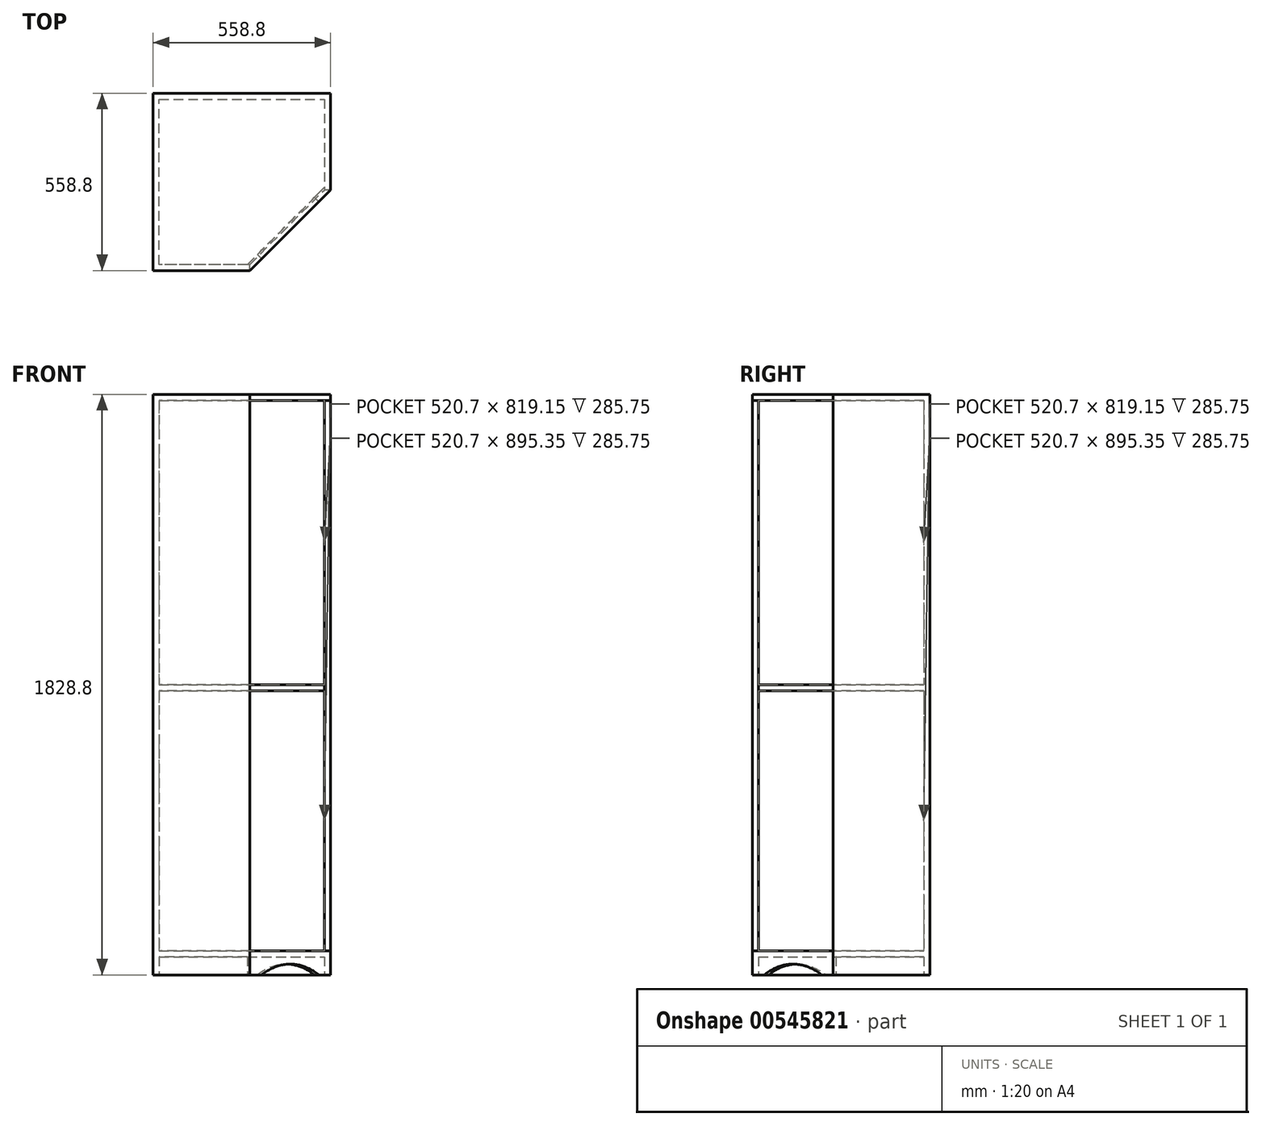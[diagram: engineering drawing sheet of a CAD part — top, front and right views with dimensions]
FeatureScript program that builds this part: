
annotation { "Feature Type Name" : "Feature", "Feature Type Description" : "" }
export const myFeature = defineFeature(function(context is Context, id is Id, definition is map)
    precondition{}
    {
        {
            var Q0;
            Q0=qCreatedBy(makeId("Top.planeOp"),FACE);
            var sketch = newSketch(context, id + "F0", { "sketchPlane" : qUnion([Q0])});
            skLineSegment(sketch, "E0", {"start": v(-279.4, 279.4) * mm, "end": v(279.4, 279.4) * mm});
            skLineSegment(sketch, "E1", {"start": v(279.4, 279.4) * mm, "end": v(279.4, -25.4) * mm});
            skLineSegment(sketch, "E2", {"start": v(279.4, -25.4) * mm, "end": v(25.4, -279.4) * mm, "construction": true});
            skLineSegment(sketch, "E3", {"start": v(25.4, -279.4) * mm, "end": v(-279.4, -279.4) * mm});
            skLineSegment(sketch, "E4", {"start": v(-279.4, -279.4) * mm, "end": v(-279.4, 279.4) * mm});
            skLineSegment(sketch, "E5", {"start": v(-279.4, -279.4) * mm, "end": v(279.4, 279.4) * mm, "construction": true});
            skLineSegment(sketch, "E6.0", {"start": v(260.35, 260.35) * mm, "end": v(260.35, -25.4) * mm});
            skLineSegment(sketch, "E6.1", {"start": v(-260.35, 260.35) * mm, "end": v(260.35, 260.35) * mm});
            skLineSegment(sketch, "E6.2", {"start": v(-260.35, -260.35) * mm, "end": v(-260.35, 260.35) * mm});
            skLineSegment(sketch, "E6.3", {"start": v(25.4, -260.35) * mm, "end": v(-260.35, -260.35) * mm});
            skLineSegment(sketch, "E7", {"start": v(279.4, -25.4) * mm, "end": v(260.35, -25.4) * mm});
            skLineSegment(sketch, "E8", {"start": v(25.4, -279.4) * mm, "end": v(25.4, -260.35) * mm});
            skSolve(sketch);
        }
        {
            var Q0;
            Q0=makeQuery(id+"F0.imprint","IMPRINT",FACE,{"disambiguationData":[TD([[makeQuery(id+"F0.imprint","IMPRINT",EDGE,{"derivedFrom":sQuery(id+"F0.wireOp",EDGE,"E0")}),-1.0]])]});
            var Q1;
            Q1 = qConstructionFilter(qBodyType(qCreatedBy(id + "F0" ,EDGE), BodyType.WIRE), ConstructionObject.NO);
            extrude(context, id + "F1", {"entities" : qUnion([Q0]), "surfaceEntities" : qUnion([Q1]), "depth" : 1828.8 * mm, "offsetDistance" : 25.4 * mm});
        }
        {
            var Q0;
            Q0=makeQuery(id+"F1.opExtrude","CAP_FACE",FACE,{"disambiguationData":[OSD([sQuery(id+"F0.wireOp",EDGE,"E0"),sQuery(id+"F0.wireOp",EDGE,"E1"),sQuery(id+"F0.wireOp",EDGE,"E3"),sQuery(id+"F0.wireOp",EDGE,"E4"),sQuery(id+"F0.wireOp",EDGE,"E6.0"),sQuery(id+"F0.wireOp",EDGE,"E6.1"),sQuery(id+"F0.wireOp",EDGE,"E6.2"),sQuery(id+"F0.wireOp",EDGE,"E6.3"),sQuery(id+"F0.wireOp",EDGE,"E7"),sQuery(id+"F0.wireOp",EDGE,"E8")])],"isStart":false});
            var sketch = newSketch(context, id + "F2", { "sketchPlane" : qUnion([Q0])});
            skLineSegment(sketch, "E9", {"start": v(25.4, -279.4) * mm, "end": v(279.4, -25.4) * mm});
            skLineSegment(sketch, "E10.0", {"start": v(25.4, -279.4) * mm, "end": v(-279.4, -279.4) * mm});
            skLineSegment(sketch, "E10.1", {"start": v(-279.4, -279.4) * mm, "end": v(-279.4, 279.4) * mm});
            skLineSegment(sketch, "E10.2", {"start": v(-279.4, 279.4) * mm, "end": v(279.4, 279.4) * mm});
            skLineSegment(sketch, "E10.3", {"start": v(279.4, 279.4) * mm, "end": v(279.4, -25.4) * mm});
            skSolve(sketch);
        }
        {
            var Q0;
            Q0 = qSketchRegion(id + "F2", true);
            extrude(context, id + "F3", {"entities" : qUnion([Q0]), "operationType" : NewBodyOperationType.ADD, "oppositeDirection" : true, "depth" : 19.05 * mm, "offsetDistance" : 25.4 * mm});
        }
        {
            var Q0;
            Q0=qCreatedBy(makeId("Top.planeOp"),FACE);
            var sketch = newSketch(context, id + "F4", { "sketchPlane" : qUnion([Q0])});
            skLineSegment(sketch, "E11.0", {"start": v(25.4, -279.4) * mm, "end": v(-279.4, -279.4) * mm});
            skLineSegment(sketch, "E11.1", {"start": v(279.4, 279.4) * mm, "end": v(279.4, -25.4) * mm});
            skLineSegment(sketch, "E11.2", {"start": v(-279.4, 279.4) * mm, "end": v(279.4, 279.4) * mm});
            skLineSegment(sketch, "E11.3", {"start": v(-279.4, -279.4) * mm, "end": v(-279.4, 279.4) * mm});
            skLineSegment(sketch, "E12", {"start": v(25.4, -279.4) * mm, "end": v(279.4, -25.4) * mm});
            skSolve(sketch);
        }
        {
            var Q0;
            Q0 = qSketchRegion(id + "F4", true);
            extrude(context, id + "F5", {"entities" : qUnion([Q0]), "operationType" : NewBodyOperationType.ADD, "depth" : 76.2 * mm, "offsetDistance" : 25.4 * mm});
        }
        {
            var Q0;
            Q0=makeQuery(id+"F5.boolean.opBoolean","MERGE",FACE,{"derivedFrom":[makeQuery(id+"F1.opExtrude","CAP_FACE",FACE,{"disambiguationData":[OSD([sQuery(id+"F0.wireOp",EDGE,"E0"),sQuery(id+"F0.wireOp",EDGE,"E1"),sQuery(id+"F0.wireOp",EDGE,"E3"),sQuery(id+"F0.wireOp",EDGE,"E4"),sQuery(id+"F0.wireOp",EDGE,"E6.0"),sQuery(id+"F0.wireOp",EDGE,"E6.1"),sQuery(id+"F0.wireOp",EDGE,"E6.2"),sQuery(id+"F0.wireOp",EDGE,"E6.3"),sQuery(id+"F0.wireOp",EDGE,"E7"),sQuery(id+"F0.wireOp",EDGE,"E8")])],"isStart":true}),makeQuery(id+"F5.opExtrude","CAP_FACE",FACE,{"disambiguationData":[OSD([sQuery(id+"F4.wireOp",EDGE,"E11.0"),sQuery(id+"F4.wireOp",EDGE,"E11.1"),sQuery(id+"F4.wireOp",EDGE,"E11.2"),sQuery(id+"F4.wireOp",EDGE,"E11.3"),sQuery(id+"F4.wireOp",EDGE,"E12")])],"isStart":true})]});
            var sketch = newSketch(context, id + "F6", { "sketchPlane" : qUnion([Q0])});
            skLineSegment(sketch, "E13.0", {"start": v(260.35, -260.35) * mm, "end": v(260.35, 17.5) * mm});
            skLineSegment(sketch, "E13.1", {"start": v(17.5, 260.35) * mm, "end": v(260.35, 17.5) * mm});
            skLineSegment(sketch, "E13.2", {"start": v(-260.35, -260.35) * mm, "end": v(260.35, -260.35) * mm});
            skLineSegment(sketch, "E13.3", {"start": v(-260.35, 260.35) * mm, "end": v(-260.35, -260.35) * mm});
            skLineSegment(sketch, "E13.4", {"start": v(17.5, 260.35) * mm, "end": v(-260.35, 260.35) * mm});
            skSolve(sketch);
        }
        {
            var Q0;
            Q0 = qSketchRegion(id + "F6", true);
            extrude(context, id + "F7", {"entities" : qUnion([Q0]), "operationType" : NewBodyOperationType.REMOVE, "oppositeDirection" : true, "depth" : 57.15 * mm, "offsetDistance" : 25.4 * mm});
        }
        {
            var Q0;
            Q0=makeQuery(id+"F5.opExtrude","SWEPT_FACE",FACE,{"disambiguationData":[OSD([sQuery(id+"F4.wireOp",EDGE,"E12")])]});
            var sketch = newSketch(context, id + "F8", { "sketchPlane" : qUnion([Q0])});
            skArc(sketch, "E14", {"start": v(127, 0) * mm, "mid": v(0, 34.03) * mm, "end": v(-127, 0) * mm});
            skPoint(sketch, "E14.centerSnap0", {"position": v(0, 0) * mm});
            skLineSegment(sketch, "E15.0", {"start": v(-127, 0) * mm, "end": v(127, 0) * mm});
            skPoint(sketch, "E16.orphan", {"position": v(-179.6, 0) * mm});
            skPoint(sketch, "E17.orphan", {"position": v(179.6, 0) * mm});
            skSolve(sketch);
        }
        {
            var Q0;
            Q0 = qSketchRegion(id + "F8", true);
            extrude(context, id + "F9", {"entities" : qUnion([Q0]), "operationType" : NewBodyOperationType.REMOVE, "oppositeDirection" : true, "depth" : 25.4 * mm, "offsetDistance" : 25.4 * mm});
        }
        {
            var Q0;
            Q0=makeQuery(id+"F5.boolean.opBoolean","MERGE",FACE,{"derivedFrom":[makeQuery(id+"F1.opExtrude","CAP_FACE",FACE,{"disambiguationData":[OSD([sQuery(id+"F0.wireOp",EDGE,"E0"),sQuery(id+"F0.wireOp",EDGE,"E1"),sQuery(id+"F0.wireOp",EDGE,"E3"),sQuery(id+"F0.wireOp",EDGE,"E4"),sQuery(id+"F0.wireOp",EDGE,"E6.0"),sQuery(id+"F0.wireOp",EDGE,"E6.1"),sQuery(id+"F0.wireOp",EDGE,"E6.2"),sQuery(id+"F0.wireOp",EDGE,"E6.3"),sQuery(id+"F0.wireOp",EDGE,"E7"),sQuery(id+"F0.wireOp",EDGE,"E8")])],"isStart":true}),makeQuery(id+"F5.opExtrude","CAP_FACE",FACE,{"disambiguationData":[OSD([sQuery(id+"F4.wireOp",EDGE,"E11.0"),sQuery(id+"F4.wireOp",EDGE,"E11.1"),sQuery(id+"F4.wireOp",EDGE,"E11.2"),sQuery(id+"F4.wireOp",EDGE,"E11.3"),sQuery(id+"F4.wireOp",EDGE,"E12")])],"isStart":true})]});
            cPlane(context, id + "F10", {"entities" : qUnion([Q0]), "cplaneType" : CPlaneType.OFFSET, "offset" : 914.4 * mm, "oppositeDirection" : true, "width" : 152.4 * mm, "height" : 152.4 * mm});
        }
        {
            var Q0;
            Q0=qCreatedBy(id+"F10.planeOp",FACE);
            var sketch = newSketch(context, id + "F11", { "sketchPlane" : qUnion([Q0])});
            skLineSegment(sketch, "E18.0.1", {"start": v(-260.35, -260.35) * mm, "end": v(260.35, -260.35) * mm});
            skLineSegment(sketch, "E18.0.3", {"start": v(260.35, -260.35) * mm, "end": v(-260.35, -260.35) * mm});
            skLineSegment(sketch, "E18.1.1", {"start": v(-260.35, 260.35) * mm, "end": v(-260.35, -260.35) * mm});
            skLineSegment(sketch, "E18.1.3", {"start": v(-260.35, -260.35) * mm, "end": v(-260.35, 260.35) * mm});
            skLineSegment(sketch, "E18.2.1", {"start": v(25.4, 260.35) * mm, "end": v(-260.35, 260.35) * mm});
            skLineSegment(sketch, "E18.2.3", {"start": v(-260.35, 260.35) * mm, "end": v(25.4, 260.35) * mm});
            skLineSegment(sketch, "E18.3.1", {"start": v(260.35, -260.35) * mm, "end": v(260.35, 25.4) * mm});
            skLineSegment(sketch, "E18.3.3", {"start": v(260.35, 25.4) * mm, "end": v(260.35, -260.35) * mm});
            skLineSegment(sketch, "E19", {"start": v(25.4, 260.35) * mm, "end": v(260.35, 25.4) * mm});
            skSolve(sketch);
        }
        {
            var Q0;
            Q0 = qSketchRegion(id + "F11", true);
            extrude(context, id + "F12", {"entities" : qUnion([Q0]), "operationType" : NewBodyOperationType.ADD, "depth" : 19.05 * mm, "offsetDistance" : 25.4 * mm});
        }
    });
